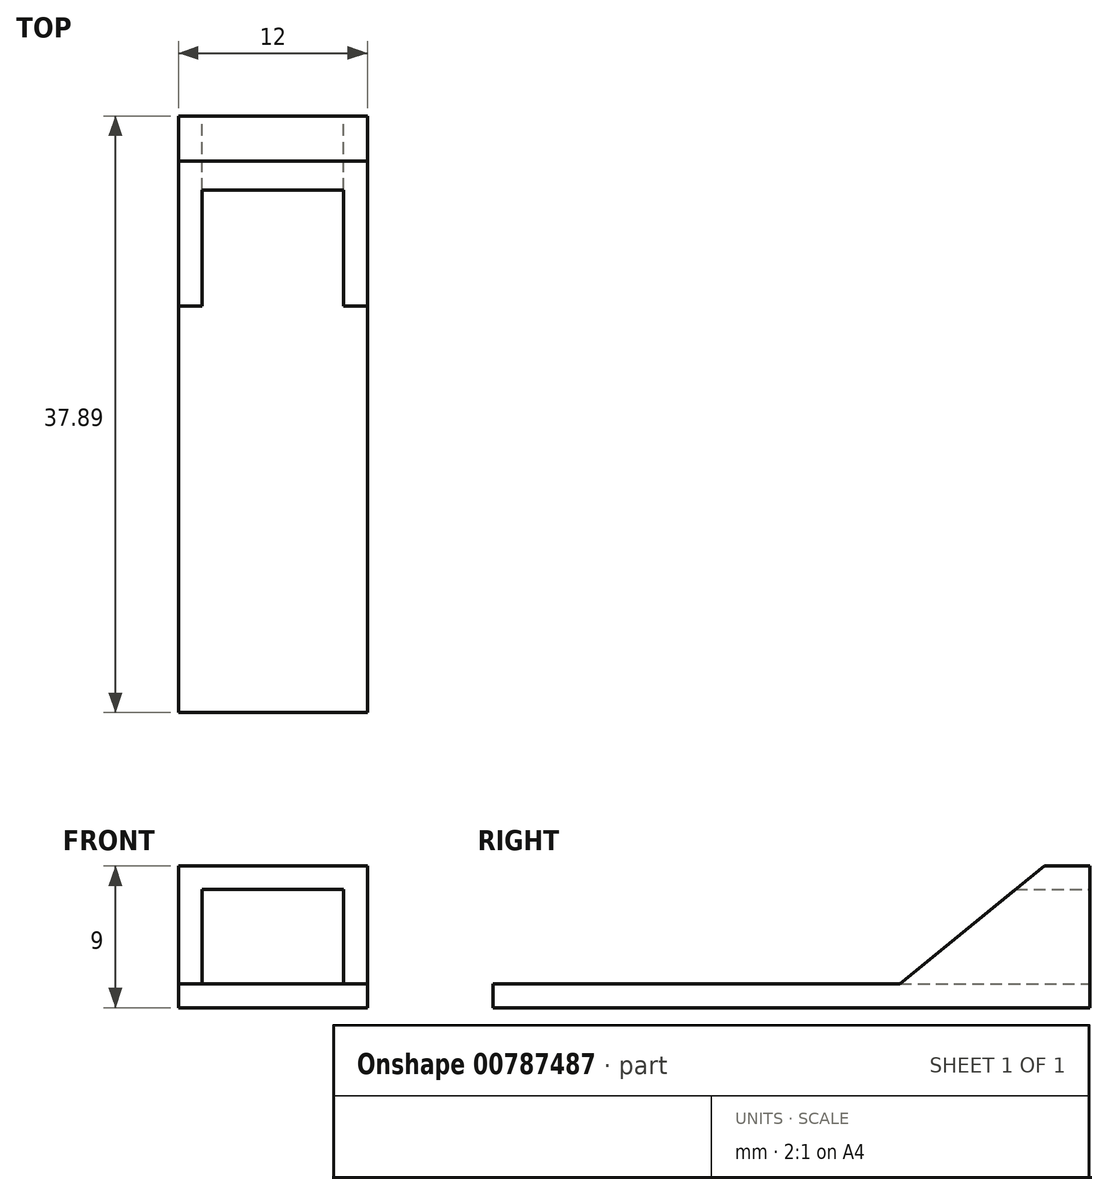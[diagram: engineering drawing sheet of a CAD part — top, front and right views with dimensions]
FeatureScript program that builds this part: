
annotation { "Feature Type Name" : "Feature", "Feature Type Description" : "" }
export const myFeature = defineFeature(function(context is Context, id is Id, definition is map)
    precondition{}
    {
        {
            var Q0;
            Q0=qCreatedBy(makeId("Right.planeOp"),FACE);
            var sketch = newSketch(context, id + "F0", { "sketchPlane" : qUnion([Q0])});
            skLineSegment(sketch, "E0", {"start": v(8.7, 0) * mm, "end": v(8.7, 9) * mm});
            skLineSegment(sketch, "E1", {"start": v(8.7, 9) * mm, "end": v(5.84, 9) * mm});
            skLineSegment(sketch, "E2", {"start": v(5.84, 9) * mm, "end": v(-3.36, 1.5) * mm});
            skLineSegment(sketch, "E3", {"start": v(-3.36, 1.5) * mm, "end": v(-29.18, 1.5) * mm});
            skLineSegment(sketch, "E4", {"start": v(-29.18, 1.5) * mm, "end": v(-29.18, 0) * mm});
            skLineSegment(sketch, "E5", {"start": v(-29.18, 0) * mm, "end": v(8.7, 0) * mm});
            skSolve(sketch);
        }
        {
            var Q0;
            Q0=makeQuery(id+"F0.imprint","IMPRINT",FACE,{"disambiguationData":[TD([[makeQuery(id+"F0.imprint","IMPRINT",EDGE,{"derivedFrom":sQuery(id+"F0.wireOp",EDGE,"E0")}),1.0]])]});
            extrude(context, id + "F1", {"entities" : qUnion([Q0]), "endBound" : BoundingType.SYMMETRIC, "depth" : 12 * mm, "offsetDistance" : 25 * mm});
        }
        {
            var Q0;
            Q0=makeQuery(id+"F1.opExtrude","SWEPT_FACE",FACE,{"disambiguationData":[OSD([sQuery(id+"F0.wireOp",EDGE,"E0")])]});
            var sketch = newSketch(context, id + "F2", { "sketchPlane" : qUnion([Q0])});
            skLineSegment(sketch, "E6.bottom", {"start": v(-4.5, 7.5) * mm, "end": v(4.5, 7.5) * mm});
            skLineSegment(sketch, "E6.top", {"start": v(-4.5, 1.5) * mm, "end": v(4.5, 1.5) * mm});
            skLineSegment(sketch, "E6.left", {"start": v(-4.5, 7.5) * mm, "end": v(-4.5, 1.5) * mm});
            skLineSegment(sketch, "E6.right", {"start": v(4.5, 7.5) * mm, "end": v(4.5, 1.5) * mm});
            skSolve(sketch);
        }
        {
            var Q0;
            Q0=makeQuery(id+"F2.imprint","IMPRINT",FACE,{"disambiguationData":[TD([[makeQuery(id+"F2.imprint","IMPRINT",EDGE,{"derivedFrom":sQuery(id+"F2.wireOp",EDGE,"E6.bottom")}),-1.0]])]});
            var Q1;
            Q1=makeQuery(id+"F1.opExtrude","SWEPT_FACE",FACE,{"disambiguationData":[OSD([sQuery(id+"F0.wireOp",EDGE,"E2")])]});
            extrude(context, id + "F3", {"entities" : qUnion([Q0]), "operationType" : NewBodyOperationType.REMOVE, "endBound" : BoundingType.UP_TO_SURFACE, "oppositeDirection" : true, "depth" : 25 * mm, "endBoundEntityFace" : qUnion([Q1]), "offsetDistance" : 25 * mm});
        }
    });
